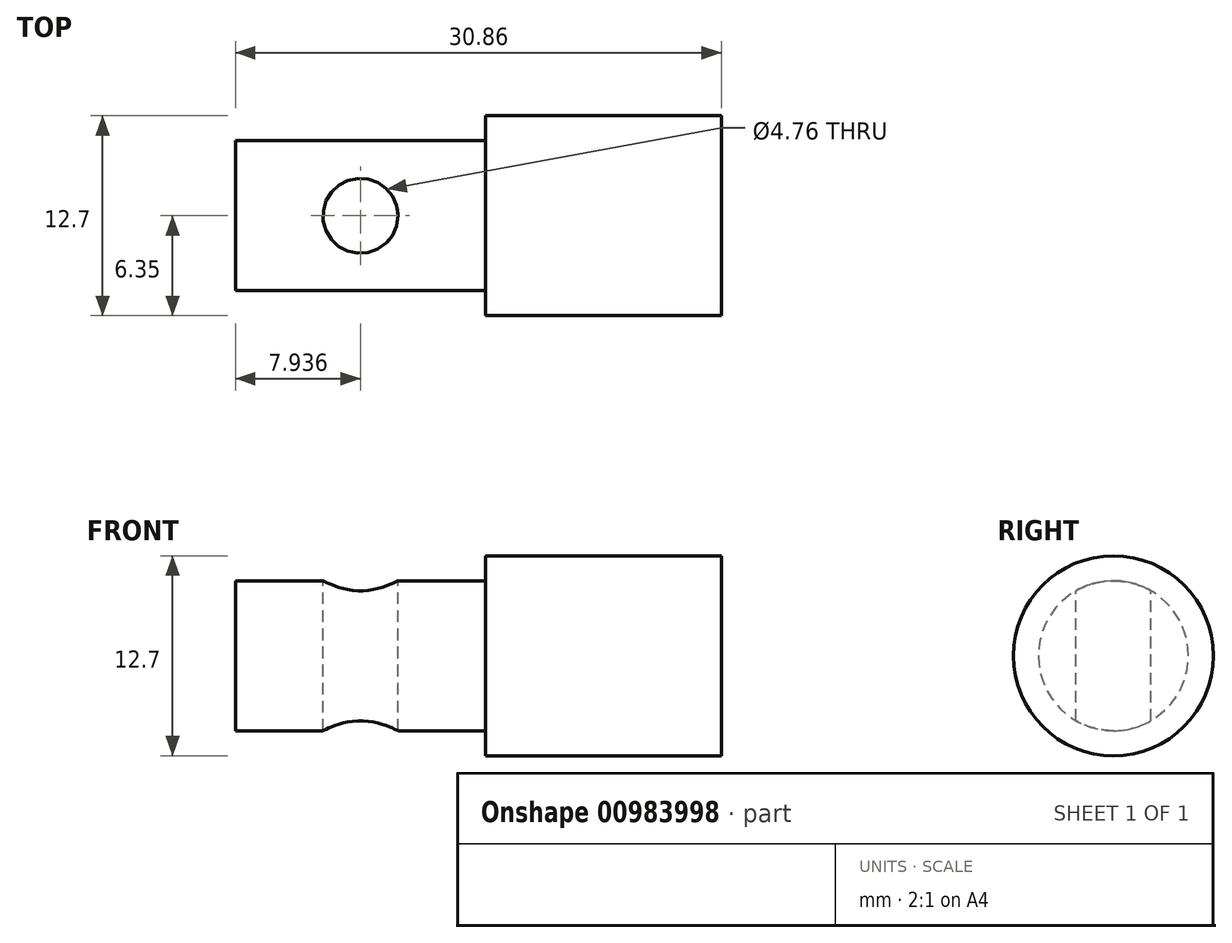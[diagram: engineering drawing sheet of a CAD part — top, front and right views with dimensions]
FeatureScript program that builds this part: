
annotation { "Feature Type Name" : "Feature", "Feature Type Description" : "" }
export const myFeature = defineFeature(function(context is Context, id is Id, definition is map)
    precondition{}
    {
        {
            var Q0;
            Q0=qCreatedBy(makeId("Front.planeOp"),FACE);
            var sketch = newSketch(context, id + "F0", { "sketchPlane" : qUnion([Q0])});
            skLineSegment(sketch, "E0", {"start": v(0, 0) * mm, "end": v(-145.94, 0) * mm, "construction": true});
            skLineSegment(sketch, "E1", {"start": v(0, 0) * mm, "end": v(0, 6.35) * mm});
            skLineSegment(sketch, "E2", {"start": v(0, 6.35) * mm, "end": v(-14.99, 6.35) * mm});
            skLineSegment(sketch, "E3", {"start": v(-14.99, 6.35) * mm, "end": v(-14.99, 4.76) * mm});
            skLineSegment(sketch, "E4", {"start": v(-14.99, 4.76) * mm, "end": v(-30.86, 4.76) * mm});
            skLineSegment(sketch, "E5", {"start": v(-30.86, 4.76) * mm, "end": v(-30.86, 0) * mm});
            skLineSegment(sketch, "E6", {"start": v(-30.86, 0) * mm, "end": v(0, 0) * mm});
            skSolve(sketch);
        }
        {
            var Q0;
            Q0 = qSketchRegion(id + "F0", true);
            var Q1;
            Q1=sQuery(id+"F0.wireOp",EDGE,"E0");
            revolve(context, id + "F1", {"surfaceOperationType" : NewSurfaceOperationType.NEW, "entities" : qUnion([Q0]), "axis" : qUnion([Q1]), "revolveType" : RevolveType.FULL});
        }
        {
            var Q0;
            Q0=qCreatedBy(makeId("Top.planeOp"),FACE);
            var sketch = newSketch(context, id + "F2", { "sketchPlane" : qUnion([Q0])});
            skPoint(sketch, "E7", {"position": v(-22.92, 0) * mm});
            skCircle(sketch, "E8", {"center": v(-22.92, 0) * mm, "radius": 2.38 * mm});
            skSolve(sketch);
        }
        {
            var Q0;
            Q0 = qSketchRegion(id + "F2", true);
            extrude(context, id + "F3", {"entities" : qUnion([Q0]), "operationType" : NewBodyOperationType.REMOVE, "endBound" : BoundingType.SYMMETRIC, "oppositeDirection" : true, "depth" : 50.8 * mm, "offsetDistance" : 25.4 * mm});
        }
    });
